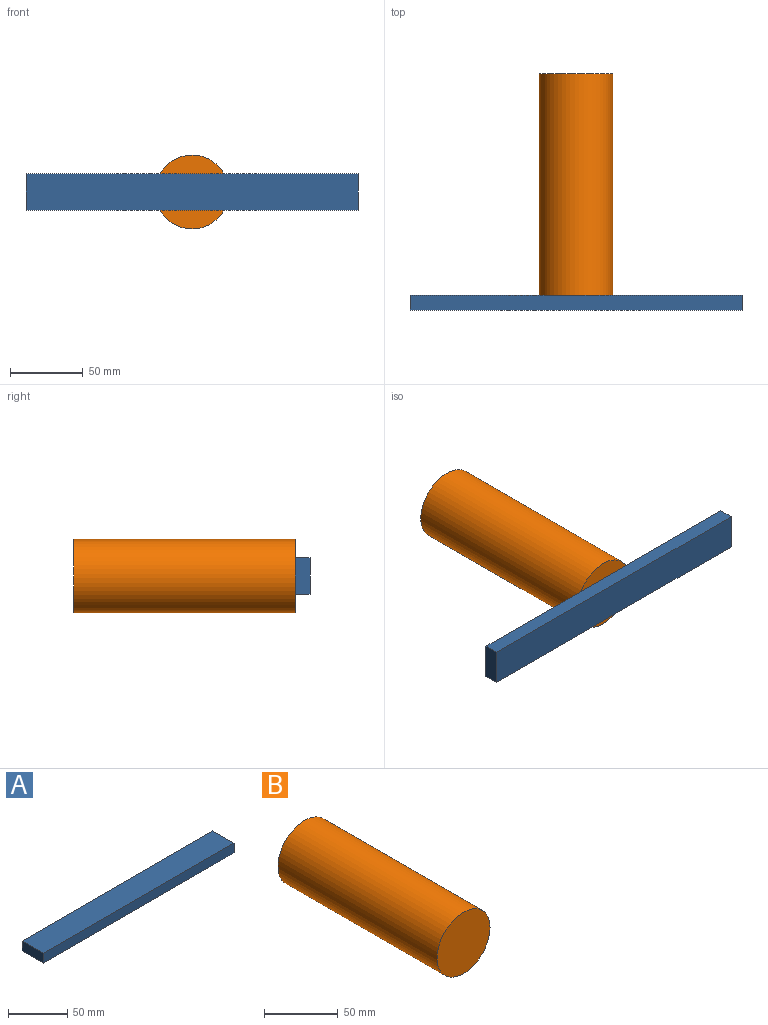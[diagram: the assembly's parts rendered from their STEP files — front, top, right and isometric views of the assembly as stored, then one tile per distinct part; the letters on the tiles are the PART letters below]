
ASSEMBLY  parts=2 mates=1
PART A: 6 faces, bbox 228.6x25.4x10.2 mm
  f0: plane 228.6x25.4mm, normal (0,0,-1), area 5806.4mm2, adj f1,f3,f4,f5
  f1: plane 25.4x10.16mm, normal (1,0,0), area 258.1mm2, adj f0,f2,f4,f5
  f2: plane 228.6x25.4mm, normal (0,0,1), area 5806.4mm2, adj f1,f3,f4,f5
  f3: plane 25.4x10.16mm, normal (-1,0,0), area 258.1mm2, adj f0,f2,f4,f5
  f4: plane 228.6x10.16mm, normal (0,-1,0), area 2322.6mm2, adj f0,f1,f2,f3
  f5: plane 228.6x10.16mm, normal (0,1,0), area 2322.6mm2, adj f0,f1,f2,f3
PART B: 3 faces, bbox 50.8x152.4x50.8 mm
  f0: cylinder r=25.4mm len=152.4mm, axis (0,1,0), area 24322mm2, adj f1,f2
  f1: plane 50.8x50.8mm, normal (0,-1,0), area 2026.8mm2, adj f0
  f2: plane 50.8x50.8mm, normal (0,1,0), area 2026.8mm2, adj f0
PLACE A rot(axis=(-1,0,0),90deg) t=(49.57,-125.53,-10.28)mm
PLACE B t=(4.84,76.2,2.42)mm
MATE slider A.f2 <-> B.f0  axis (0,1,0) through (4.84,-76.2,2.42)mm
